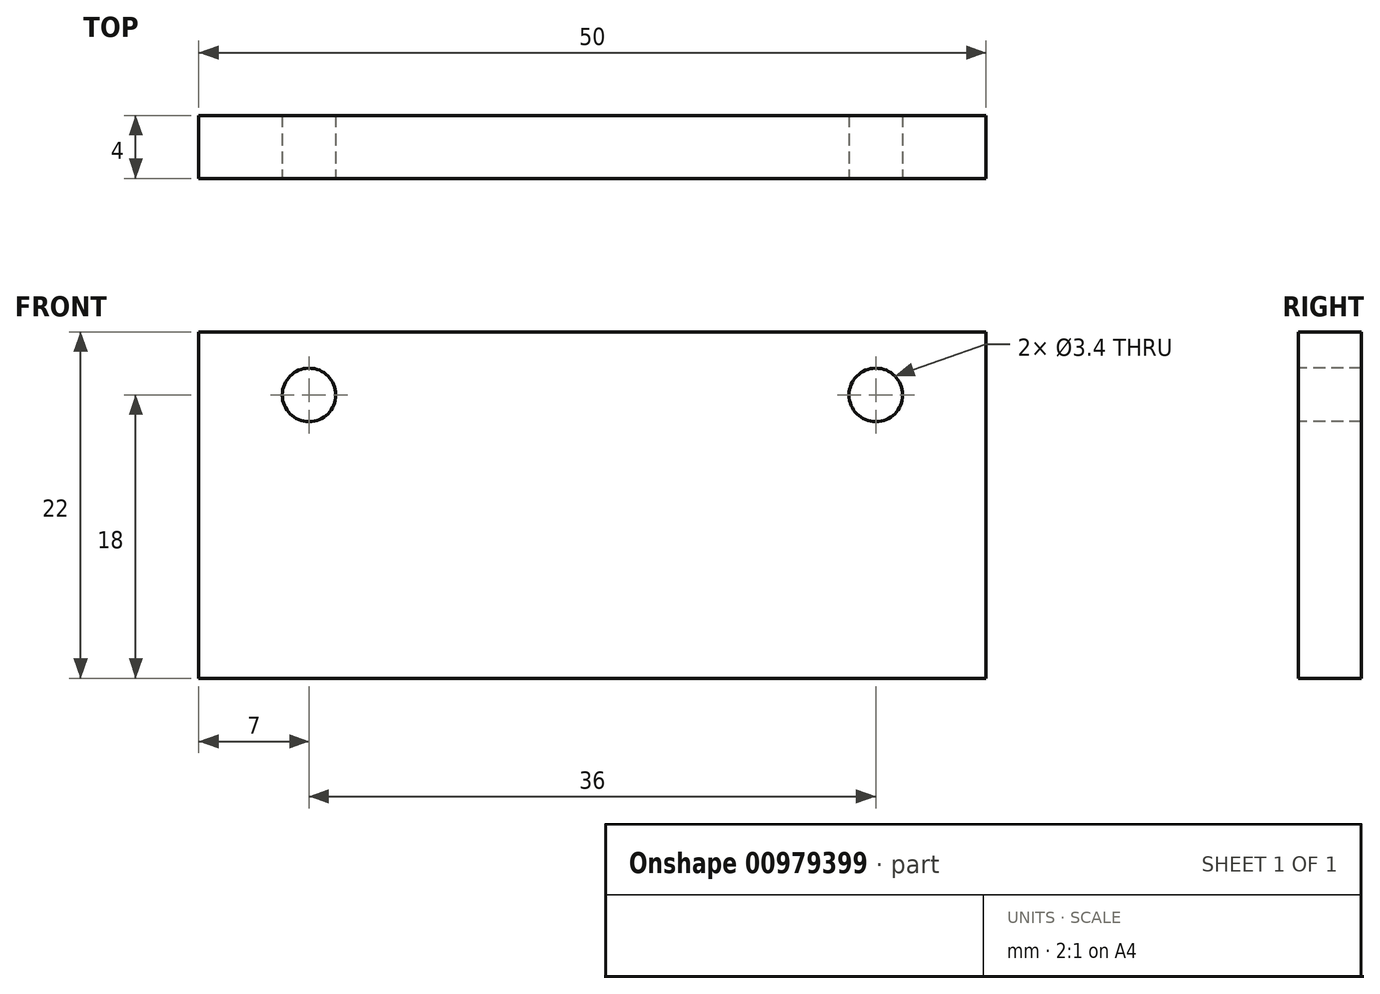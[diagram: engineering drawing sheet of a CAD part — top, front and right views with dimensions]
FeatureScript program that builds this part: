
annotation { "Feature Type Name" : "Feature", "Feature Type Description" : "" }
export const myFeature = defineFeature(function(context is Context, id is Id, definition is map)
    precondition{}
    {
        {
            var Q0;
            Q0=qCreatedBy(makeId("Front.planeOp"),FACE);
            var sketch = newSketch(context, id + "F0", { "sketchPlane" : qUnion([Q0])});
            skLineSegment(sketch, "E0.bottom", {"start": v(0, 0) * mm, "end": v(50, 0) * mm});
            skLineSegment(sketch, "E0.top", {"start": v(0, 22) * mm, "end": v(50, 22) * mm});
            skLineSegment(sketch, "E0.left", {"start": v(0, 0) * mm, "end": v(0, 22) * mm});
            skLineSegment(sketch, "E0.right", {"start": v(50, 0) * mm, "end": v(50, 22) * mm});
            skSolve(sketch);
        }
        {
            var Q0;
            Q0=makeQuery(id+"F0.imprint","IMPRINT",FACE,{"disambiguationData":[TD([[makeQuery(id+"F0.imprint","IMPRINT",EDGE,{"derivedFrom":sQuery(id+"F0.wireOp",EDGE,"E0.bottom")}),1.0]])]});
            extrude(context, id + "F1", {"entities" : qUnion([Q0]), "depth" : 4 * mm, "offsetDistance" : 25 * mm});
        }
        {
            var Q0;
            Q0=makeQuery(id+"F1.opExtrude","CAP_FACE",FACE,{"disambiguationData":[OSD([sQuery(id+"F0.wireOp",EDGE,"E0.bottom"),sQuery(id+"F0.wireOp",EDGE,"E0.top"),sQuery(id+"F0.wireOp",EDGE,"E0.left"),sQuery(id+"F0.wireOp",EDGE,"E0.right")])],"isStart":false});
            var sketch = newSketch(context, id + "F2", { "sketchPlane" : qUnion([Q0])});
            skPoint(sketch, "E1", {"position": v(7, 18) * mm});
            skPoint(sketch, "E2", {"position": v(43, 18) * mm});
            skSolve(sketch);
        }
        {
            var Q0;
            Q0=sQuery(id+"F2.wireOp",VERTEX,"E1");
            var Q1;
            Q1=sQuery(id+"F2.wireOp",VERTEX,"E2");
            var Q2;
            Q2=makeQuery(id+"F1.opExtrude","SWEPT_BODY",BODY,{"disambiguationData":[OSD([sQuery(id+"F0.wireOp",EDGE,"E0.bottom"),sQuery(id+"F0.wireOp",EDGE,"E0.top"),sQuery(id+"F0.wireOp",EDGE,"E0.left"),sQuery(id+"F0.wireOp",EDGE,"E0.right")])]});
            hole(context, id + "F3", {"style" : HoleStyle.SIMPLE, "endStyle" : HoleEndStyle.THROUGH, "standardTappedOrClearance" : lookupTablePath({ "fit" : "Normal", "standard" : "ISO", "size" : "M3", "type" : "Clearance" }), "standardBlindInLast" : lookupTablePath({ "fit" : "Normal", "standard" : "ISO", "engagement" : "75%", "pitch" : "0.5 mm", "size" : "M3", "type" : "Clearance & tapped" }), "holeDiameter" : 3.4 * mm, "majorDiameter" : 5 * mm, "isTappedThrough" : true, "tappedDepth" : 12.6 * mm, "tapClearance" : 3, "startFromSketch" : true, "locations" : qUnion([Q0, Q1]), "scope" : qUnion([Q2])});
        }
    });
